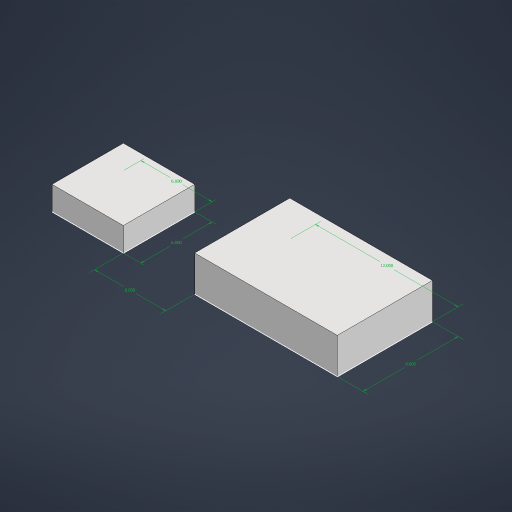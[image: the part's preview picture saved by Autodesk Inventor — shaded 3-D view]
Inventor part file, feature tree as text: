
AUTODESK INVENTOR PART (.ipt)
format: ipt  version: 2023.1 (Build 271208000, 208)  size: 178,176 bytes
history: native  units: in
note: dims shown in document units (in); Inventor stores cm internally (conversion verified against a paired STEP export)
features: extrude x2, sketch x1
ambient origin geometry x8: Origin, YZ Plane, XZ Plane, XY Plane, X Axis, Y Axis, Z Axis, Center Point
bodies: Solid1 (feature_tree), Solid2 (feature_tree)
feature tree (3):
  sketch  "Sketch2"  dims[d3=6.0in d4=6.0in d5=2.0in d6=0.0in d7=12.0in d8=8.0in d9=6.0in d10=3.0in d11=0.0in]
  extrude  "Extrusion1"  Depth=6.0in
  extrude  "Extrusion2"  Depth=2.0in TaperAngle=0.0deg
